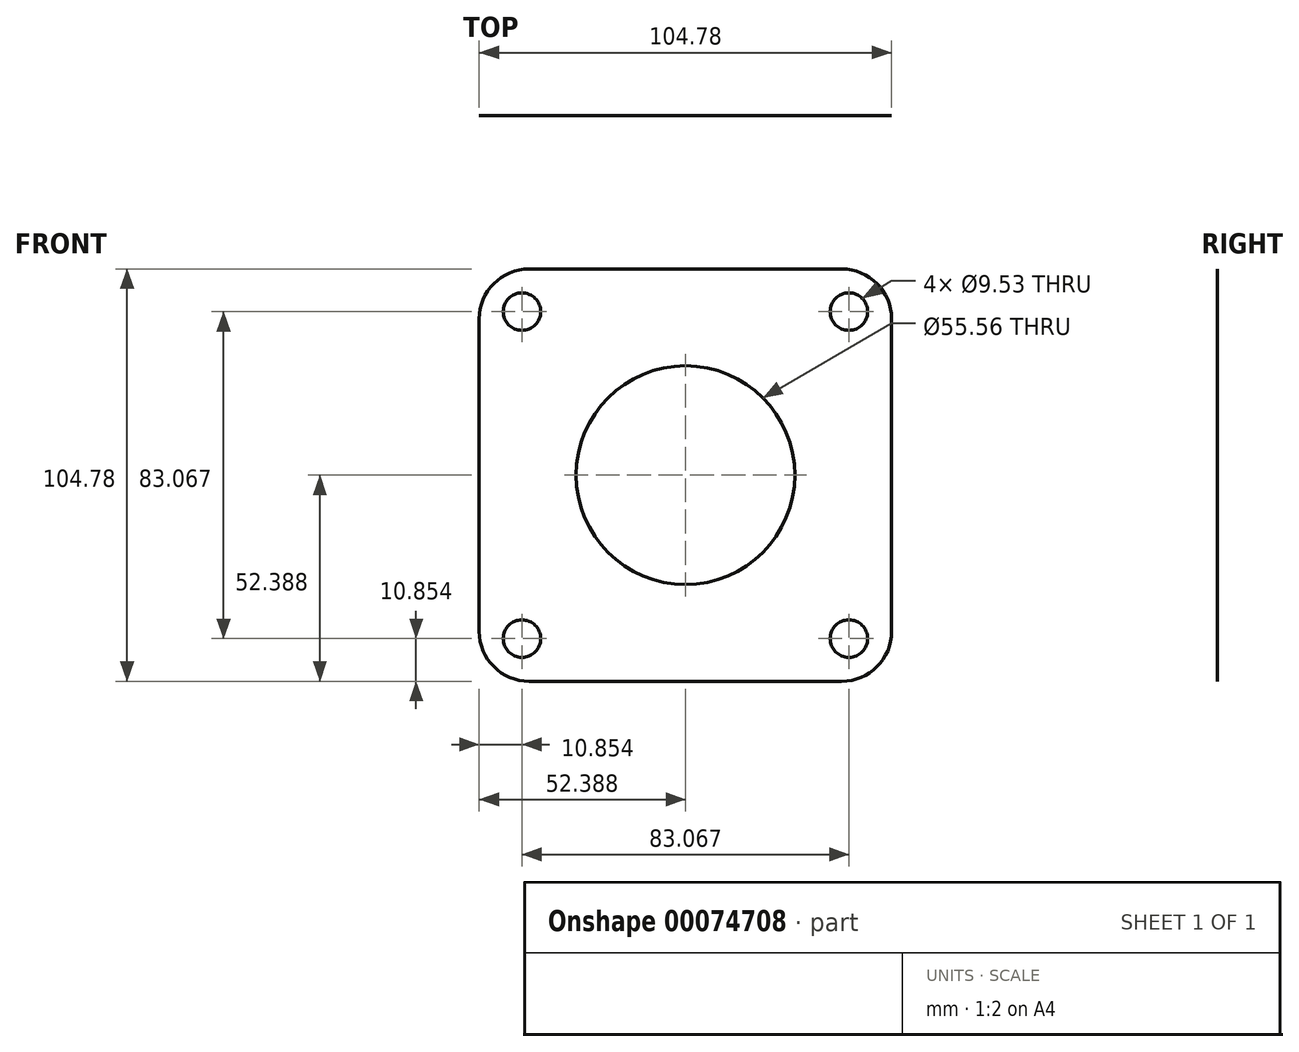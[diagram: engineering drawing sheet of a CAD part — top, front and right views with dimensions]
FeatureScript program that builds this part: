
annotation { "Feature Type Name" : "Feature", "Feature Type Description" : "" }
export const myFeature = defineFeature(function(context is Context, id is Id, definition is map)
    precondition{}
    {
        {
            var Q0;
            Q0=qCreatedBy(makeId("Front.planeOp"),FACE);
            var sketch = newSketch(context, id + "F0", { "sketchPlane" : qUnion([Q0])});
            skLineSegment(sketch, "E0.bottom", {"start": v(12.7, 0) * mm, "end": v(92.08, 0) * mm});
            skLineSegment(sketch, "E0.top", {"start": v(12.7, 104.77) * mm, "end": v(92.07, 104.77) * mm});
            skLineSegment(sketch, "E0.left", {"start": v(0, 12.7) * mm, "end": v(0, 92.08) * mm});
            skLineSegment(sketch, "E0.right", {"start": v(104.78, 12.7) * mm, "end": v(104.77, 92.07) * mm});
            skCircle(sketch, "E1", {"center": v(52.39, 52.39) * mm, "radius": 27.78 * mm});
            skPoint(sketch, "E1.centerSnap0", {"position": v(52.39, 0) * mm});
            skPoint(sketch, "E1.centerSnap1", {"position": v(0, 52.39) * mm});
            skLineSegment(sketch, "E2", {"start": v(52.39, 52.39) * mm, "end": v(0, 104.77) * mm, "construction": true});
            skCircle(sketch, "E3", {"center": v(10.85, 93.92) * mm, "radius": 4.76 * mm});
            skCircle(sketch, "E4.1.0", {"center": v(10.85, 10.85) * mm, "radius": 4.76 * mm});
            skCircle(sketch, "E4.2.0", {"center": v(93.92, 10.85) * mm, "radius": 4.76 * mm});
            skCircle(sketch, "E4.3.0", {"center": v(93.92, 93.92) * mm, "radius": 4.76 * mm});
            skPoint(sketch, "E5.visualSharp", {"position": v(0, 104.77) * mm});
            skArc(sketch, "E5.filletArc", {"start": v(12.7, 104.78) * mm, "mid": v(3.72, 101.06) * mm, "end": v(0, 92.08) * mm});
            skPoint(sketch, "E6.visualSharp", {"position": v(104.77, 104.77) * mm});
            skArc(sketch, "E6.filletArc", {"start": v(104.77, 92.07) * mm, "mid": v(101.06, 101.06) * mm, "end": v(92.07, 104.77) * mm});
            skPoint(sketch, "E7.visualSharp", {"position": v(0, 0) * mm});
            skArc(sketch, "E7.filletArc", {"start": v(0, 12.7) * mm, "mid": v(3.72, 3.72) * mm, "end": v(12.7, 0) * mm});
            skPoint(sketch, "E8.visualSharp", {"position": v(104.78, 0) * mm});
            skArc(sketch, "E8.filletArc", {"start": v(92.08, 0) * mm, "mid": v(101.06, 3.72) * mm, "end": v(104.78, 12.7) * mm});
            skSolve(sketch);
        }
        {
            var Q0;
            Q0=makeQuery(id+"F0.imprint","IMPRINT",FACE,{"disambiguationData":[TD([[makeQuery(id+"F0.imprint","IMPRINT",EDGE,{"derivedFrom":sQuery(id+"F0.wireOp",EDGE,"E0.bottom")}),1.0]])]});
            extrude(context, id + "F1", {"entities" : qUnion([Q0]), "depth" : 1 / 406.4 * mm});
        }
    });
